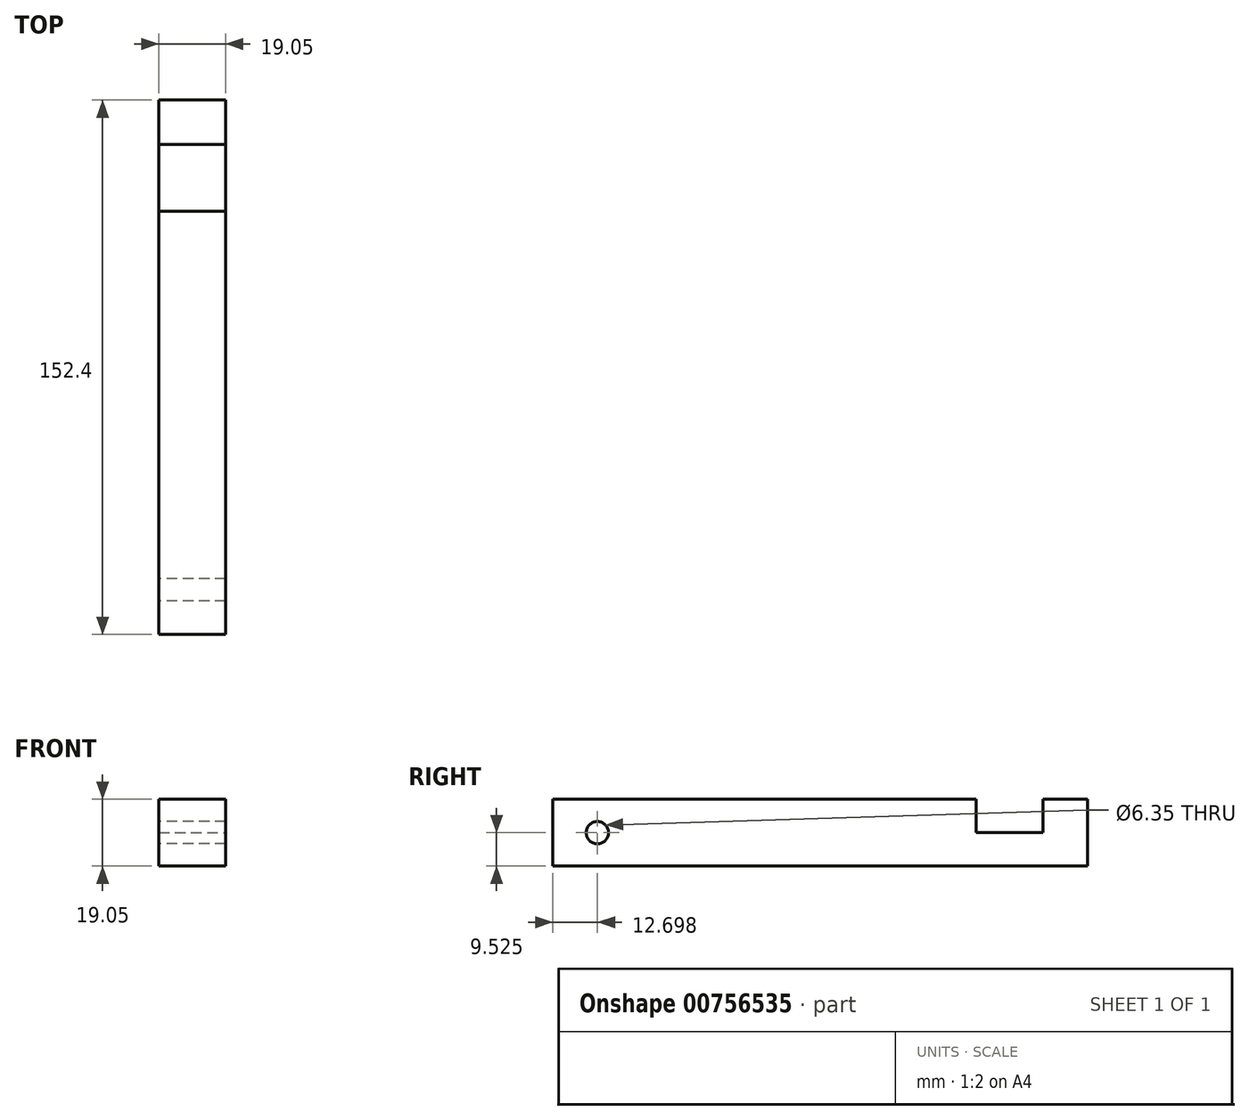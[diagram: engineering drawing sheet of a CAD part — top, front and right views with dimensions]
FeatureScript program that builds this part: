
annotation { "Feature Type Name" : "Feature", "Feature Type Description" : "" }
export const myFeature = defineFeature(function(context is Context, id is Id, definition is map)
    precondition{}
    {
        {
            var Q0;
            Q0=qCreatedBy(makeId("Top.planeOp"),FACE);
            var sketch = newSketch(context, id + "F0", { "sketchPlane" : qUnion([Q0])});
            skLineSegment(sketch, "E0.bottom", {"start": v(-35.19, 110.12) * mm, "end": v(-16.14, 110.12) * mm});
            skLineSegment(sketch, "E0.top", {"start": v(-35.19, -42.28) * mm, "end": v(-16.14, -42.28) * mm});
            skLineSegment(sketch, "E0.left", {"start": v(-35.19, 110.12) * mm, "end": v(-35.19, -42.28) * mm});
            skLineSegment(sketch, "E0.right", {"start": v(-16.14, 110.12) * mm, "end": v(-16.14, -42.28) * mm});
            skLineSegment(sketch, "E1.bottom", {"start": v(-35.19, 97.42) * mm, "end": v(-16.14, 97.42) * mm});
            skLineSegment(sketch, "E1.top", {"start": v(-35.19, 78.37) * mm, "end": v(-16.14, 78.37) * mm});
            skLineSegment(sketch, "E1.left", {"start": v(-35.19, 97.42) * mm, "end": v(-35.19, 78.37) * mm});
            skLineSegment(sketch, "E1.right", {"start": v(-16.14, 97.42) * mm, "end": v(-16.14, 78.37) * mm});
            skSolve(sketch);
        }
        {
            var Q0;
            Q0=makeQuery(id+"F0.imprint","IMPRINT",FACE,{"disambiguationData":[TD([[makeQuery(id+"F0.imprint","IMPRINT",EDGE,{"derivedFrom":sQuery(id+"F0.wireOp",EDGE,"E1.bottom")}),-1.0]])]});
            extrude(context, id + "F1", {"entities" : qUnion([Q0]), "depth" : 9.52 * mm, "offsetDistance" : 25.4 * mm});
        }
        {
            var Q0;
            {var subQ0=sQuery(id+"F0.wireOp",EDGE,"E0.top");Q0=makeQuery(id+"F0.imprint","IMPRINT",FACE,{"disambiguationData":[TD([[makeQuery(id+"F0.imprint","IMPRINT",EDGE,{"derivedFrom":subQ0}),1.0]])]});}
            var Q1;
            {var subQ0=sQuery(id+"F0.wireOp",EDGE,"E0.bottom");Q1=makeQuery(id+"F0.imprint","IMPRINT",FACE,{"disambiguationData":[TD([[makeQuery(id+"F0.imprint","IMPRINT",EDGE,{"derivedFrom":subQ0}),-1.0]])]});}
            extrude(context, id + "F2", {"entities" : qUnion([Q0, Q1]), "operationType" : NewBodyOperationType.ADD, "depth" : 19.05 * mm, "offsetDistance" : 25.4 * mm});
        }
        {
            var Q0;
            {var subQ0=sQuery(id+"F0.wireOp",EDGE,"E0.left");var subQ1=sQuery(id+"F0.wireOp",EDGE,"E1.left");Q0=makeQuery(id+"F2.boolean.opBoolean","MERGE",FACE,{"derivedFrom":[makeQuery(id+"F1.opExtrude","SWEPT_FACE",FACE,{"disambiguationData":[OSD([subQ1])]}),makeQuery(id+"F2.opExtrude","SWEPT_FACE",FACE,{"disambiguationData":[OSD([subQ0]),TDD([makeQuery(id+"F0.imprint","IMPRINT",EDGE,{"disambiguationData":[TD([[makeQuery(id+"F0.imprint","INTERSECT",VERTEX,{"derivedFrom":[sQuery(id+"F0.wireOp",EDGE,"E0.bottom"),subQ0]}),-1.0]])],"derivedFrom":subQ0})])]}),makeQuery(id+"F2.opExtrude","SWEPT_FACE",FACE,{"disambiguationData":[OSD([subQ0]),TDD([makeQuery(id+"F0.imprint","IMPRINT",EDGE,{"disambiguationData":[TD([[makeQuery(id+"F0.imprint","INTERSECT",VERTEX,{"derivedFrom":[sQuery(id+"F0.wireOp",EDGE,"E0.top"),subQ0]}),1.0]])],"derivedFrom":subQ0})])]})]});}
            var sketch = newSketch(context, id + "F3", { "sketchPlane" : qUnion([Q0])});
            skCircle(sketch, "E2", {"center": v(29.58, 9.53) * mm, "radius": 3.2 * mm});
            skSolve(sketch);
        }
        {
            var Q0;
            Q0=sQuery(id+"F3.wireOp",VERTEX,"E2.center");
            var Q1;
            Q1=makeQuery(id+"F1.opExtrude","SWEPT_BODY",BODY,{"disambiguationData":[OSD([sQuery(id+"F0.wireOp",EDGE,"E1.bottom"),sQuery(id+"F0.wireOp",EDGE,"E1.top"),sQuery(id+"F0.wireOp",EDGE,"E1.left"),sQuery(id+"F0.wireOp",EDGE,"E1.right")])]});
            hole(context, id + "F4", {"style" : HoleStyle.SIMPLE, "endStyle" : HoleEndStyle.THROUGH, "holeDiameter" : 6.35 * mm, "majorDiameter" : 6.35 * mm, "isTappedThrough" : true, "tappedDepth" : 12.7 * mm, "tapClearance" : 3, "locations" : qUnion([Q0]), "scope" : qUnion([Q1])});
        }
    });
